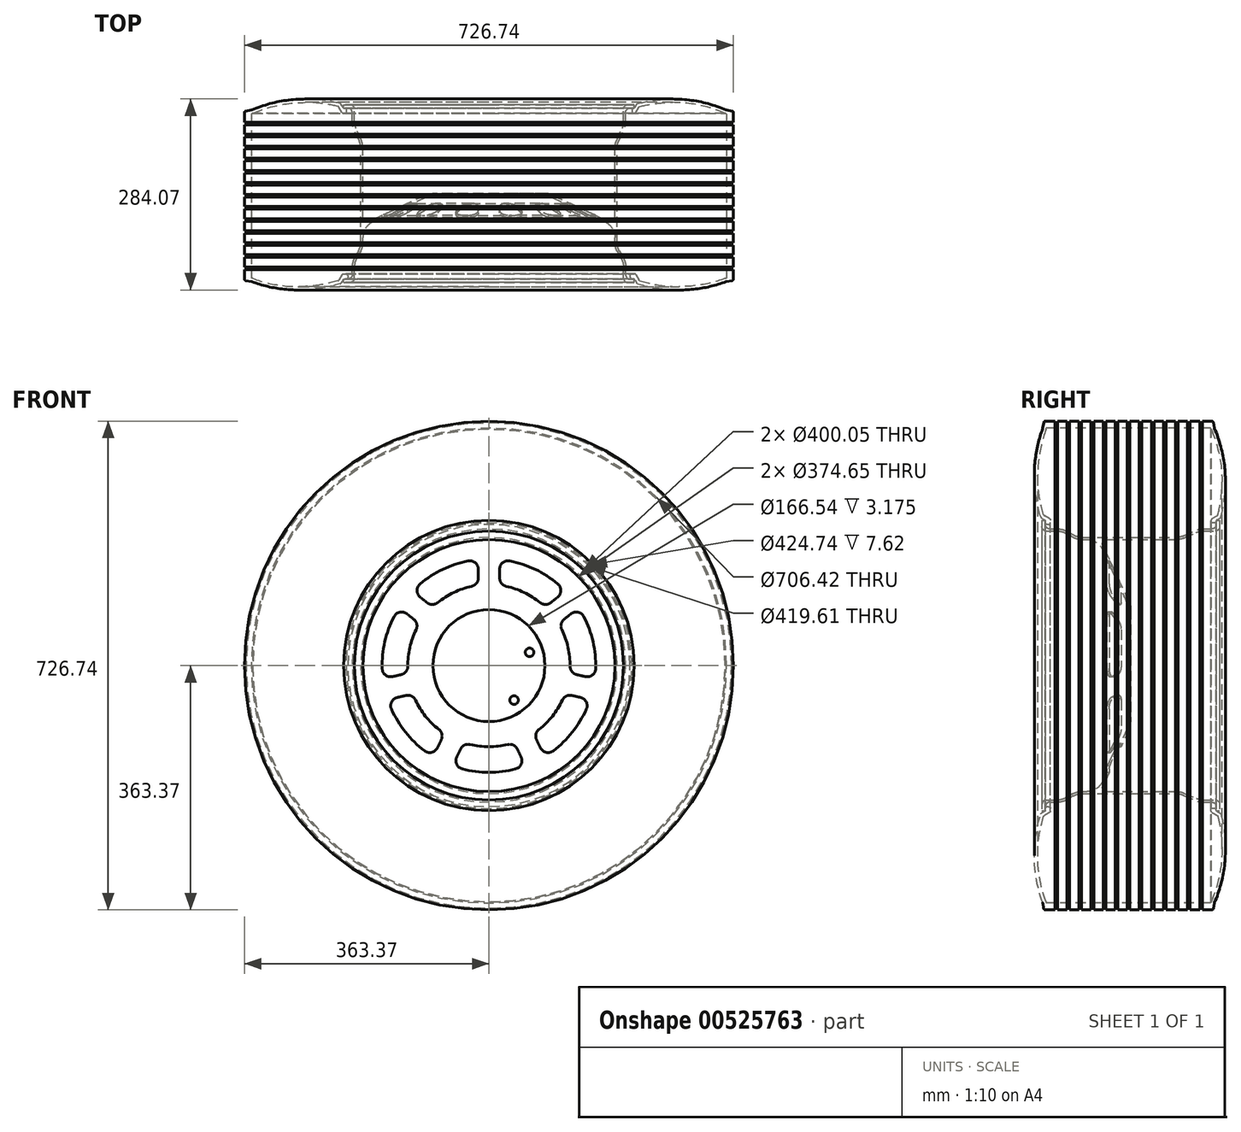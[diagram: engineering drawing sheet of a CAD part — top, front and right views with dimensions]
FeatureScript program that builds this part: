
annotation { "Feature Type Name" : "Feature", "Feature Type Description" : "" }
export const myFeature = defineFeature(function(context is Context, id is Id, definition is map)
    precondition{}
    {
        {
            var Q0;
            Q0=qCreatedBy(makeId("Top.planeOp"),FACE);
            var sketch = newSketch(context, id + "F0", { "sketchPlane" : qUnion([Q0])});
            skLineSegment(sketch, "E0", {"start": v(0, 0) * mm, "end": v(83.27, 0) * mm});
            skLineSegment(sketch, "E1", {"start": v(94, -2.38) * mm, "end": v(172.66, -39.06) * mm});
            skLineSegment(sketch, "E2", {"start": v(200.02, -106.01) * mm, "end": v(200.02, -122.55) * mm});
            skLineSegment(sketch, "E3", {"start": v(206.38, -128.9) * mm, "end": v(215.9, -128.9) * mm});
            skLineSegment(sketch, "E4", {"start": v(215.9, -128.9) * mm, "end": v(215.9, -123.82) * mm});
            skLineSegment(sketch, "E5", {"start": v(215.9, -123.82) * mm, "end": v(209.55, -123.82) * mm});
            skLineSegment(sketch, "E6", {"start": v(190.5, -69.45) * mm, "end": v(190.5, 70.8) * mm});
            skLineSegment(sketch, "E7", {"start": v(192.69, 81.13) * mm, "end": v(202.65, 103.54) * mm});
            skLineSegment(sketch, "E8", {"start": v(203.2, 106.12) * mm, "end": v(203.2, 123.83) * mm});
            skLineSegment(sketch, "E9", {"start": v(209.55, 130.18) * mm, "end": v(215.9, 130.18) * mm});
            skLineSegment(sketch, "E10", {"start": v(215.9, 130.18) * mm, "end": v(215.9, 135.26) * mm});
            skLineSegment(sketch, "E11", {"start": v(215.9, 135.26) * mm, "end": v(206.37, 135.26) * mm});
            skLineSegment(sketch, "E12", {"start": v(200.03, 128.9) * mm, "end": v(200.03, 110.84) * mm});
            skLineSegment(sketch, "E13", {"start": v(197.84, 100.52) * mm, "end": v(189.51, 81.8) * mm});
            skLineSegment(sketch, "E14", {"start": v(187.33, 71.48) * mm, "end": v(187.33, -32.43) * mm});
            skLineSegment(sketch, "E15", {"start": v(178.3, -38.18) * mm, "end": v(94.7, 0.8) * mm});
            skLineSegment(sketch, "E16", {"start": v(83.97, 3.18) * mm, "end": v(0, 3.17) * mm});
            skLineSegment(sketch, "E17", {"start": v(0, 3.17) * mm, "end": v(0, 0) * mm});
            skPoint(sketch, "E18.end.orphan", {"position": v(203.2, -45.9) * mm});
            skLineSegment(sketch, "E19", {"start": v(190.67, -82.9) * mm, "end": v(196.68, -93.41) * mm});
            skLineSegment(sketch, "E20", {"start": v(193.85, -82.06) * mm, "end": v(199.85, -92.57) * mm});
            skLineSegment(sketch, "E21", {"start": v(203.2, -105.17) * mm, "end": v(203.2, -117.47) * mm});
            skLineSegment(sketch, "E22.trimOffspring", {"start": v(187.33, -62.08) * mm, "end": v(187.33, -70.3) * mm});
            skPoint(sketch, "E23", {"position": v(190.5, 0) * mm});
            skPoint(sketch, "E24", {"position": v(190.5, -76.2) * mm});
            skPoint(sketch, "E25.visualSharp", {"position": v(88.9, 0) * mm});
            skArc(sketch, "E25.filletArc", {"start": v(94, -2.38) * mm, "mid": v(88.77, -0.6) * mm, "end": v(83.27, 0) * mm});
            skPoint(sketch, "E26.visualSharp", {"position": v(89.6, 3.18) * mm});
            skArc(sketch, "E26.filletArc", {"start": v(94.7, 0.8) * mm, "mid": v(89.47, 2.57) * mm, "end": v(83.97, 3.18) * mm});
            skPoint(sketch, "E27.visualSharp", {"position": v(187.33, -45.9) * mm});
            skArc(sketch, "E27.filletArc", {"start": v(187.32, -62.08) * mm, "mid": v(183.35, -48.43) * mm, "end": v(172.66, -39.06) * mm});
            skPoint(sketch, "E28.visualSharp", {"position": v(187.33, -42.4) * mm});
            skArc(sketch, "E28.filletArc", {"start": v(178.3, -38.18) * mm, "mid": v(184.39, -37.78) * mm, "end": v(187.33, -32.43) * mm});
            skArc(sketch, "E29.filletArc", {"start": v(190.5, -69.45) * mm, "mid": v(191.35, -75.97) * mm, "end": v(193.85, -82.06) * mm});
            skPoint(sketch, "E30.visualSharp", {"position": v(187.33, -77.04) * mm});
            skArc(sketch, "E30.filletArc", {"start": v(187.33, -70.3) * mm, "mid": v(188.18, -76.82) * mm, "end": v(190.67, -82.9) * mm});
            skPoint(sketch, "E31.visualSharp", {"position": v(200.02, -99.27) * mm});
            skArc(sketch, "E31.filletArc", {"start": v(200.02, -106.01) * mm, "mid": v(199.17, -99.5) * mm, "end": v(196.68, -93.41) * mm});
            skPoint(sketch, "E32.visualSharp", {"position": v(203.2, -98.42) * mm});
            skArc(sketch, "E32.filletArc", {"start": v(203.2, -105.17) * mm, "mid": v(202.35, -98.65) * mm, "end": v(199.85, -92.57) * mm});
            skPoint(sketch, "E33.visualSharp", {"position": v(190.5, 76.2) * mm});
            skArc(sketch, "E33.filletArc", {"start": v(192.69, 81.13) * mm, "mid": v(191.05, 76.08) * mm, "end": v(190.5, 70.8) * mm});
            skPoint(sketch, "E34.visualSharp", {"position": v(187.33, 76.87) * mm});
            skArc(sketch, "E34.filletArc", {"start": v(189.51, 81.8) * mm, "mid": v(187.88, 76.76) * mm, "end": v(187.33, 71.48) * mm});
            skPoint(sketch, "E35.visualSharp", {"position": v(200.03, 105.45) * mm});
            skArc(sketch, "E35.filletArc", {"start": v(197.84, 100.52) * mm, "mid": v(199.47, 105.57) * mm, "end": v(200.03, 110.84) * mm});
            skPoint(sketch, "E36.visualSharp", {"position": v(203.2, 104.78) * mm});
            skArc(sketch, "E36.filletArc", {"start": v(202.65, 103.54) * mm, "mid": v(203.06, 104.8) * mm, "end": v(203.2, 106.12) * mm});
            skPoint(sketch, "E37.visualSharp", {"position": v(203.2, 130.18) * mm});
            skArc(sketch, "E37.filletArc", {"start": v(209.55, 130.18) * mm, "mid": v(205.06, 128.32) * mm, "end": v(203.2, 123.83) * mm});
            skPoint(sketch, "E38.visualSharp", {"position": v(200.03, 135.26) * mm});
            skArc(sketch, "E38.filletArc", {"start": v(206.37, 135.26) * mm, "mid": v(201.88, 133.4) * mm, "end": v(200.02, 128.9) * mm});
            skPoint(sketch, "E39.visualSharp", {"position": v(203.2, -123.82) * mm});
            skArc(sketch, "E39.filletArc", {"start": v(203.2, -117.47) * mm, "mid": v(205.06, -121.97) * mm, "end": v(209.55, -123.82) * mm});
            skPoint(sketch, "E40.visualSharp", {"position": v(200.02, -128.9) * mm});
            skArc(sketch, "E40.filletArc", {"start": v(200.03, -122.55) * mm, "mid": v(201.88, -127.05) * mm, "end": v(206.38, -128.9) * mm});
            skSolve(sketch);
        }
        {
            var Q0;
            Q0=qCreatedBy(makeId("Top.planeOp"),FACE);
            var sketch = newSketch(context, id + "F1", { "sketchPlane" : qUnion([Q0])});
            skLineSegment(sketch, "E41", {"start": v(212.37, 130.18) * mm, "end": v(214.69, 130.18) * mm});
            skLineSegment(sketch, "E42", {"start": v(216.89, 131.45) * mm, "end": v(219.44, 135.86) * mm});
            skArc(sketch, "E43", {"start": v(352.47, 127.57) * mm, "mid": v(287.52, 143.27) * mm, "end": v(220.99, 137.05) * mm});
            skLineSegment(sketch, "E44", {"start": v(353.03, 127.4) * mm, "end": v(361.27, 125.95) * mm});
            skLineSegment(sketch, "E45", {"start": v(363.37, 123.45) * mm, "end": v(363.37, 109.33) * mm});
            skLineSegment(sketch, "E46", {"start": v(361.27, -126.25) * mm, "end": v(352.96, -127.71) * mm});
            skArc(sketch, "E47", {"start": v(220.9, -130.73) * mm, "mid": v(286.96, -140.23) * mm, "end": v(352.53, -127.83) * mm});
            skLineSegment(sketch, "E48", {"start": v(219.47, -129.57) * mm, "end": v(216.89, -125.1) * mm});
            skLineSegment(sketch, "E49", {"start": v(214.69, -123.82) * mm, "end": v(212.34, -123.82) * mm});
            skLineSegment(sketch, "E50", {"start": v(212.37, 130.18) * mm, "end": v(212.37, 122.56) * mm});
            skLineSegment(sketch, "E51", {"start": v(212.37, 122.56) * mm, "end": v(216.15, 122.56) * mm});
            skLineSegment(sketch, "E52", {"start": v(218.35, 123.83) * mm, "end": v(222.77, 131.48) * mm});
            skArc(sketch, "E53", {"start": v(351, 122.67) * mm, "mid": v(288.5, 138.1) * mm, "end": v(224.35, 132.67) * mm});
            skLineSegment(sketch, "E54", {"start": v(351.11, 122.58) * mm, "end": v(351.57, 122.5) * mm});
            skLineSegment(sketch, "E55", {"start": v(353.2, 120.08) * mm, "end": v(353.2, -122.09) * mm});
            skLineSegment(sketch, "E56", {"start": v(352.8, -122.59) * mm, "end": v(351.63, -122.8) * mm});
            skArc(sketch, "E57", {"start": v(224.34, -126.48) * mm, "mid": v(288.06, -135.12) * mm, "end": v(351.2, -122.9) * mm});
            skLineSegment(sketch, "E58", {"start": v(222.88, -125.32) * mm, "end": v(218.35, -117.47) * mm});
            skLineSegment(sketch, "E59", {"start": v(216.15, -116.2) * mm, "end": v(212.34, -116.2) * mm});
            skLineSegment(sketch, "E60", {"start": v(209.8, -118.74) * mm, "end": v(209.8, -121.28) * mm});
            skPoint(sketch, "E61.visualSharp", {"position": v(217.62, 122.56) * mm});
            skArc(sketch, "E61.filletArc", {"start": v(216.15, 122.56) * mm, "mid": v(217.42, 122.9) * mm, "end": v(218.35, 123.83) * mm});
            skPoint(sketch, "E62.visualSharp", {"position": v(216.15, 130.18) * mm});
            skArc(sketch, "E62.filletArc", {"start": v(214.69, 130.18) * mm, "mid": v(215.96, 130.52) * mm, "end": v(216.89, 131.45) * mm});
            skPoint(sketch, "E63.visualSharp", {"position": v(223.3, 132.4) * mm});
            skArc(sketch, "E63.filletArc", {"start": v(224.35, 132.67) * mm, "mid": v(223.44, 132.23) * mm, "end": v(222.77, 131.48) * mm});
            skPoint(sketch, "E64.visualSharp", {"position": v(219.96, 136.77) * mm});
            skArc(sketch, "E64.filletArc", {"start": v(220.99, 137.05) * mm, "mid": v(220.1, 136.6) * mm, "end": v(219.44, 135.86) * mm});
            skPoint(sketch, "E65.visualSharp", {"position": v(352.74, 127.46) * mm});
            skArc(sketch, "E65.filletArc", {"start": v(352.47, 127.57) * mm, "mid": v(352.74, 127.47) * mm, "end": v(353.03, 127.4) * mm});
            skPoint(sketch, "E66.visualSharp", {"position": v(351.28, 122.56) * mm});
            skArc(sketch, "E66.filletArc", {"start": v(351, 122.67) * mm, "mid": v(351.28, 122.57) * mm, "end": v(351.57, 122.5) * mm});
            skPoint(sketch, "E67.visualSharp", {"position": v(353.2, 122.21) * mm});
            skArc(sketch, "E67.filletArc", {"start": v(353.2, 120.08) * mm, "mid": v(352.62, 121.72) * mm, "end": v(351.11, 122.58) * mm});
            skPoint(sketch, "E68.visualSharp", {"position": v(363.37, 125.58) * mm});
            skArc(sketch, "E68.filletArc", {"start": v(363.37, 123.45) * mm, "mid": v(362.78, 125.08) * mm, "end": v(361.27, 125.95) * mm});
            skPoint(sketch, "E69.visualSharp", {"position": v(363.37, -125.88) * mm});
            skArc(sketch, "E69.filletArc", {"start": v(361.27, -126.25) * mm, "mid": v(362.78, -125.38) * mm, "end": v(363.37, -123.75) * mm});
            skPoint(sketch, "E70.visualSharp", {"position": v(353.2, -122.51) * mm});
            skArc(sketch, "E70.filletArc", {"start": v(352.8, -122.59) * mm, "mid": v(353.1, -122.41) * mm, "end": v(353.2, -122.09) * mm});
            skPoint(sketch, "E71.visualSharp", {"position": v(352.74, -127.75) * mm});
            skArc(sketch, "E71.filletArc", {"start": v(352.96, -127.71) * mm, "mid": v(352.74, -127.76) * mm, "end": v(352.53, -127.83) * mm});
            skPoint(sketch, "E72.visualSharp", {"position": v(351.4, -122.83) * mm});
            skArc(sketch, "E72.filletArc", {"start": v(351.63, -122.8) * mm, "mid": v(351.4, -122.84) * mm, "end": v(351.2, -122.9) * mm});
            skPoint(sketch, "E73.visualSharp", {"position": v(219.96, -130.42) * mm});
            skArc(sketch, "E73.filletArc", {"start": v(219.47, -129.57) * mm, "mid": v(220.08, -130.28) * mm, "end": v(220.9, -130.73) * mm});
            skPoint(sketch, "E74.visualSharp", {"position": v(223.38, -126.18) * mm});
            skArc(sketch, "E74.filletArc", {"start": v(222.88, -125.32) * mm, "mid": v(223.5, -126.03) * mm, "end": v(224.34, -126.48) * mm});
            skPoint(sketch, "E75.visualSharp", {"position": v(216.15, -123.82) * mm});
            skArc(sketch, "E75.filletArc", {"start": v(216.89, -125.1) * mm, "mid": v(215.96, -124.17) * mm, "end": v(214.69, -123.82) * mm});
            skPoint(sketch, "E76.visualSharp", {"position": v(209.8, -116.2) * mm});
            skArc(sketch, "E76.filletArc", {"start": v(212.34, -116.2) * mm, "mid": v(210.55, -116.95) * mm, "end": v(209.8, -118.74) * mm});
            skPoint(sketch, "E77.visualSharp", {"position": v(217.62, -116.2) * mm});
            skArc(sketch, "E77.filletArc", {"start": v(218.35, -117.47) * mm, "mid": v(217.42, -116.55) * mm, "end": v(216.15, -116.2) * mm});
            skPoint(sketch, "E78.visualSharp", {"position": v(209.8, -123.82) * mm});
            skArc(sketch, "E78.filletArc", {"start": v(209.8, -121.28) * mm, "mid": v(210.55, -123.08) * mm, "end": v(212.34, -123.82) * mm});
            skLineSegment(sketch, "E79.bottom", {"start": v(363.37, 109.33) * mm, "end": v(360.83, 109.33) * mm});
            skLineSegment(sketch, "E79.top", {"start": v(363.37, 105.52) * mm, "end": v(360.83, 105.52) * mm});
            skLineSegment(sketch, "E79.right", {"start": v(360.83, 109.33) * mm, "end": v(360.83, 105.52) * mm});
            skLineSegment(sketch, "E80.bottom", {"start": v(363.37, 91.4) * mm, "end": v(360.83, 91.4) * mm});
            skLineSegment(sketch, "E80.top", {"start": v(363.37, 87.6) * mm, "end": v(360.83, 87.6) * mm});
            skLineSegment(sketch, "E80.right", {"start": v(360.83, 91.4) * mm, "end": v(360.83, 87.6) * mm});
            skLineSegment(sketch, "E81.bottom", {"start": v(363.37, 73.47) * mm, "end": v(360.83, 73.47) * mm});
            skLineSegment(sketch, "E81.top", {"start": v(363.37, 69.66) * mm, "end": v(360.83, 69.66) * mm});
            skLineSegment(sketch, "E81.right", {"start": v(360.83, 73.47) * mm, "end": v(360.83, 69.66) * mm});
            skLineSegment(sketch, "E82.bottom", {"start": v(363.37, 55.54) * mm, "end": v(360.83, 55.54) * mm});
            skLineSegment(sketch, "E82.top", {"start": v(363.37, 51.73) * mm, "end": v(360.83, 51.73) * mm});
            skLineSegment(sketch, "E82.right", {"start": v(360.83, 55.54) * mm, "end": v(360.83, 51.73) * mm});
            skLineSegment(sketch, "E83.bottom", {"start": v(363.37, 37.61) * mm, "end": v(360.83, 37.61) * mm});
            skLineSegment(sketch, "E83.top", {"start": v(363.37, 33.8) * mm, "end": v(360.83, 33.8) * mm});
            skLineSegment(sketch, "E83.right", {"start": v(360.83, 37.61) * mm, "end": v(360.83, 33.8) * mm});
            skLineSegment(sketch, "E84.bottom", {"start": v(363.37, 19.68) * mm, "end": v(360.83, 19.68) * mm});
            skLineSegment(sketch, "E84.top", {"start": v(363.37, 15.87) * mm, "end": v(360.83, 15.87) * mm});
            skLineSegment(sketch, "E84.right", {"start": v(360.83, 19.68) * mm, "end": v(360.83, 15.87) * mm});
            skLineSegment(sketch, "E85.bottom", {"start": v(363.37, 1.75) * mm, "end": v(360.83, 1.75) * mm});
            skLineSegment(sketch, "E85.top", {"start": v(363.37, -2.06) * mm, "end": v(360.83, -2.06) * mm});
            skLineSegment(sketch, "E85.right", {"start": v(360.83, 1.75) * mm, "end": v(360.83, -2.06) * mm});
            skLineSegment(sketch, "E86.bottom", {"start": v(363.37, -16.17) * mm, "end": v(360.83, -16.17) * mm});
            skLineSegment(sketch, "E86.top", {"start": v(363.37, -19.98) * mm, "end": v(360.83, -19.98) * mm});
            skLineSegment(sketch, "E86.right", {"start": v(360.83, -16.17) * mm, "end": v(360.83, -19.98) * mm});
            skLineSegment(sketch, "E87.bottom", {"start": v(363.37, -34.1) * mm, "end": v(360.83, -34.1) * mm});
            skLineSegment(sketch, "E87.top", {"start": v(363.37, -37.91) * mm, "end": v(360.83, -37.91) * mm});
            skLineSegment(sketch, "E87.right", {"start": v(360.83, -34.1) * mm, "end": v(360.83, -37.91) * mm});
            skLineSegment(sketch, "E88.bottom", {"start": v(363.37, -52.03) * mm, "end": v(360.83, -52.03) * mm});
            skLineSegment(sketch, "E88.top", {"start": v(363.37, -55.84) * mm, "end": v(360.83, -55.84) * mm});
            skLineSegment(sketch, "E88.right", {"start": v(360.83, -52.03) * mm, "end": v(360.83, -55.84) * mm});
            skLineSegment(sketch, "E89.bottom", {"start": v(363.37, -69.96) * mm, "end": v(360.83, -69.96) * mm});
            skLineSegment(sketch, "E89.top", {"start": v(363.37, -73.77) * mm, "end": v(360.83, -73.77) * mm});
            skLineSegment(sketch, "E89.right", {"start": v(360.83, -69.96) * mm, "end": v(360.83, -73.77) * mm});
            skLineSegment(sketch, "E90.bottom", {"start": v(363.37, -87.9) * mm, "end": v(360.83, -87.9) * mm});
            skLineSegment(sketch, "E90.top", {"start": v(363.37, -91.7) * mm, "end": v(360.83, -91.7) * mm});
            skLineSegment(sketch, "E90.right", {"start": v(360.83, -87.9) * mm, "end": v(360.83, -91.7) * mm});
            skLineSegment(sketch, "E91.bottom", {"start": v(363.37, -105.82) * mm, "end": v(360.83, -105.82) * mm});
            skLineSegment(sketch, "E91.top", {"start": v(363.37, -109.63) * mm, "end": v(360.98, -109.63) * mm});
            skLineSegment(sketch, "E91.right", {"start": v(360.83, -105.82) * mm, "end": v(360.98, -109.63) * mm});
            skLineSegment(sketch, "E92.trimOffspring", {"start": v(363.37, 105.52) * mm, "end": v(363.37, 91.4) * mm});
            skLineSegment(sketch, "E93.trimOffspring", {"start": v(363.37, 87.6) * mm, "end": v(363.37, 73.47) * mm});
            skLineSegment(sketch, "E94.trimOffspring", {"start": v(363.37, 69.66) * mm, "end": v(363.37, 55.54) * mm});
            skLineSegment(sketch, "E95.trimOffspring", {"start": v(363.37, 51.73) * mm, "end": v(363.37, 37.61) * mm});
            skLineSegment(sketch, "E96.trimOffspring", {"start": v(363.37, 33.8) * mm, "end": v(363.37, 19.68) * mm});
            skLineSegment(sketch, "E97.trimOffspring", {"start": v(363.37, 15.87) * mm, "end": v(363.37, 1.75) * mm});
            skLineSegment(sketch, "E98.trimOffspring", {"start": v(363.37, -2.06) * mm, "end": v(363.37, -16.17) * mm});
            skLineSegment(sketch, "E99.trimOffspring", {"start": v(363.37, -19.98) * mm, "end": v(363.37, -34.1) * mm});
            skLineSegment(sketch, "E100.trimOffspring", {"start": v(363.37, -37.91) * mm, "end": v(363.37, -52.03) * mm});
            skLineSegment(sketch, "E101.trimOffspring", {"start": v(363.37, -73.77) * mm, "end": v(363.37, -87.9) * mm});
            skLineSegment(sketch, "E102.trimOffspring", {"start": v(363.37, -55.84) * mm, "end": v(363.37, -69.96) * mm});
            skLineSegment(sketch, "E103.trimOffspring", {"start": v(363.37, -109.63) * mm, "end": v(363.37, -123.75) * mm});
            skLineSegment(sketch, "E104.trimOffspring", {"start": v(363.37, -91.7) * mm, "end": v(363.37, -105.82) * mm});
            skLineSegment(sketch, "E105", {"start": v(0, 0) * mm, "end": v(0, 58.12) * mm, "construction": true});
            skSolve(sketch);
        }
        {
            var Q0;
            Q0=makeQuery(id+"F0.imprint","IMPRINT",FACE,{"disambiguationData":[TD([[makeQuery(id+"F0.imprint","IMPRINT",EDGE,{"derivedFrom":sQuery(id+"F0.wireOp",EDGE,"E0")}),1.0]])]});
            var Q1;
            Q1=sQuery(id+"F0.wireOp",EDGE,"E17");
            revolve(context, id + "F2", {"entities" : qUnion([Q0]), "axis" : qUnion([Q1]), "revolveType" : RevolveType.FULL});
        }
        {
            var Q0;
            Q0=makeQuery(id+"F2.opRevolve","SWEPT_FACE",FACE,{"disambiguationData":[OSD([sQuery(id+"F0.wireOp",EDGE,"E0")])]});
            var sketch = newSketch(context, id + "F3", { "sketchPlane" : qUnion([Q0])});
            skCircle(sketch, "E106", {"center": v(0, 0) * mm, "radius": 28.57 * mm});
            skCircle(sketch, "E107", {"center": v(0, 0) * mm, "radius": 63.5 * mm});
            skCircle(sketch, "E108", {"center": v(0, 63.5) * mm, "radius": 6.35 * mm});
            skCircle(sketch, "E109", {"center": v(-60.4, 19.62) * mm, "radius": 6.35 * mm});
            skCircle(sketch, "E110", {"center": v(-37.32, -51.37) * mm, "radius": 6.35 * mm});
            skCircle(sketch, "E111", {"center": v(37.32, -51.37) * mm, "radius": 6.35 * mm});
            skCircle(sketch, "E112", {"center": v(60.4, 19.62) * mm, "radius": 6.35 * mm});
            skLineSegment(sketch, "E113", {"start": v(0, 63.5) * mm, "end": v(0, 0) * mm, "construction": true});
            skLineSegment(sketch, "E114", {"start": v(60.4, 19.62) * mm, "end": v(0, 0) * mm, "construction": true});
            skLineSegment(sketch, "E115", {"start": v(0, 0) * mm, "end": v(37.32, -51.37) * mm, "construction": true});
            skLineSegment(sketch, "E116", {"start": v(0, 0) * mm, "end": v(-37.32, -51.37) * mm, "construction": true});
            skLineSegment(sketch, "E117", {"start": v(-60.4, 19.62) * mm, "end": v(0, 0) * mm, "construction": true});
            skSolve(sketch);
        }
        {
            var Q0;
            {var subQ0=sQuery(id+"F3.wireOp",EDGE,"E109");var subQ1=sQuery(id+"F3.wireOp",EDGE,"E107");var subQ2=makeQuery(id+"F3.imprint","INTERSECT",VERTEX,{"disambiguationData":[OD(0.0)],"derivedFrom":[subQ1,subQ0]});Q0=makeQuery(id+"F3.imprint","IMPRINT",FACE,{"disambiguationData":[TD([[makeQuery(id+"F3.imprint","IMPRINT",EDGE,{"disambiguationData":[TD([[subQ2,-1.0]])],"derivedFrom":subQ1}),-1.0]])]});}
            var Q1;
            {var subQ0=sQuery(id+"F3.wireOp",EDGE,"E108");var subQ1=sQuery(id+"F3.wireOp",EDGE,"E107");var subQ2=makeQuery(id+"F3.imprint","INTERSECT",VERTEX,{"disambiguationData":[OD(0.0)],"derivedFrom":[subQ1,subQ0]});Q1=makeQuery(id+"F3.imprint","IMPRINT",FACE,{"disambiguationData":[TD([[makeQuery(id+"F3.imprint","IMPRINT",EDGE,{"disambiguationData":[TD([[subQ2,-1.0]])],"derivedFrom":subQ1}),1.0]])]});}
            var Q2;
            {var subQ0=sQuery(id+"F3.wireOp",EDGE,"E112");var subQ1=sQuery(id+"F3.wireOp",EDGE,"E107");var subQ2=makeQuery(id+"F3.imprint","INTERSECT",VERTEX,{"disambiguationData":[OD(0.0)],"derivedFrom":[subQ1,subQ0]});Q2=makeQuery(id+"F3.imprint","IMPRINT",FACE,{"disambiguationData":[TD([[makeQuery(id+"F3.imprint","IMPRINT",EDGE,{"disambiguationData":[TD([[subQ2,1.0]])],"derivedFrom":subQ1}),-1.0]])]});}
            var Q3;
            {var subQ0=sQuery(id+"F3.wireOp",EDGE,"E110");var subQ1=sQuery(id+"F3.wireOp",EDGE,"E107");var subQ2=makeQuery(id+"F3.imprint","INTERSECT",VERTEX,{"disambiguationData":[OD(0.0)],"derivedFrom":[subQ1,subQ0]});Q3=makeQuery(id+"F3.imprint","IMPRINT",FACE,{"disambiguationData":[TD([[makeQuery(id+"F3.imprint","IMPRINT",EDGE,{"disambiguationData":[TD([[subQ2,-1.0]])],"derivedFrom":subQ1}),1.0]])]});}
            var Q4;
            {var subQ0=sQuery(id+"F3.wireOp",EDGE,"E111");var subQ1=sQuery(id+"F3.wireOp",EDGE,"E107");var subQ2=makeQuery(id+"F3.imprint","INTERSECT",VERTEX,{"disambiguationData":[OD(0.0)],"derivedFrom":[subQ1,subQ0]});Q4=makeQuery(id+"F3.imprint","IMPRINT",FACE,{"disambiguationData":[TD([[makeQuery(id+"F3.imprint","IMPRINT",EDGE,{"disambiguationData":[TD([[subQ2,-1.0]])],"derivedFrom":subQ1}),1.0]])]});}
            var Q5;
            {var subQ0=sQuery(id+"F3.wireOp",EDGE,"E111");var subQ1=sQuery(id+"F3.wireOp",EDGE,"E107");var subQ2=makeQuery(id+"F3.imprint","INTERSECT",VERTEX,{"disambiguationData":[OD(0.0)],"derivedFrom":[subQ1,subQ0]});Q5=makeQuery(id+"F3.imprint","IMPRINT",FACE,{"disambiguationData":[TD([[makeQuery(id+"F3.imprint","IMPRINT",EDGE,{"disambiguationData":[TD([[subQ2,-1.0]])],"derivedFrom":subQ1}),-1.0]])]});}
            var Q6;
            {var subQ0=sQuery(id+"F3.wireOp",EDGE,"E110");var subQ1=sQuery(id+"F3.wireOp",EDGE,"E107");var subQ2=makeQuery(id+"F3.imprint","INTERSECT",VERTEX,{"disambiguationData":[OD(0.0)],"derivedFrom":[subQ1,subQ0]});Q6=makeQuery(id+"F3.imprint","IMPRINT",FACE,{"disambiguationData":[TD([[makeQuery(id+"F3.imprint","IMPRINT",EDGE,{"disambiguationData":[TD([[subQ2,-1.0]])],"derivedFrom":subQ1}),-1.0]])]});}
            var Q7;
            {var subQ0=sQuery(id+"F3.wireOp",EDGE,"E112");var subQ1=sQuery(id+"F3.wireOp",EDGE,"E107");var subQ2=makeQuery(id+"F3.imprint","INTERSECT",VERTEX,{"disambiguationData":[OD(0.0)],"derivedFrom":[subQ1,subQ0]});Q7=makeQuery(id+"F3.imprint","IMPRINT",FACE,{"disambiguationData":[TD([[makeQuery(id+"F3.imprint","IMPRINT",EDGE,{"disambiguationData":[TD([[subQ2,1.0]])],"derivedFrom":subQ1}),1.0]])]});}
            var Q8;
            {var subQ0=sQuery(id+"F3.wireOp",EDGE,"E108");var subQ1=sQuery(id+"F3.wireOp",EDGE,"E107");var subQ2=makeQuery(id+"F3.imprint","INTERSECT",VERTEX,{"disambiguationData":[OD(0.0)],"derivedFrom":[subQ1,subQ0]});Q8=makeQuery(id+"F3.imprint","IMPRINT",FACE,{"disambiguationData":[TD([[makeQuery(id+"F3.imprint","IMPRINT",EDGE,{"disambiguationData":[TD([[subQ2,-1.0]])],"derivedFrom":subQ1}),-1.0]])]});}
            var Q9;
            {var subQ0=sQuery(id+"F3.wireOp",EDGE,"E109");var subQ1=sQuery(id+"F3.wireOp",EDGE,"E107");var subQ2=makeQuery(id+"F3.imprint","INTERSECT",VERTEX,{"disambiguationData":[OD(0.0)],"derivedFrom":[subQ1,subQ0]});Q9=makeQuery(id+"F3.imprint","IMPRINT",FACE,{"disambiguationData":[TD([[makeQuery(id+"F3.imprint","IMPRINT",EDGE,{"disambiguationData":[TD([[subQ2,-1.0]])],"derivedFrom":subQ1}),1.0]])]});}
            var Q10;
            Q10=makeQuery(id+"F3.imprint","IMPRINT",FACE,{"disambiguationData":[TD([[makeQuery(id+"F3.imprint","IMPRINT",EDGE,{"derivedFrom":sQuery(id+"F3.wireOp",EDGE,"E106")}),1.0]])]});
            extrude(context, id + "F4", {"entities" : qUnion([Q0, Q1, Q2, Q3, Q4, Q5, Q6, Q7, Q8, Q9, Q10]), "operationType" : NewBodyOperationType.REMOVE, "oppositeDirection" : true, "depth" : 25.4 * mm, "offsetDistance" : 25.4 * mm});
        }
        {
            var Q0;
            Q0=makeQuery(id+"F2.opRevolve","SWEPT_FACE",FACE,{"disambiguationData":[OSD([sQuery(id+"F0.wireOp",EDGE,"E0")])]});
            var sketch = newSketch(context, id + "F5", { "sketchPlane" : qUnion([Q0])});
            skArc(sketch, "E118", {"start": v(-141.08, 72.78) * mm, "mid": v(-154.77, 35.33) * mm, "end": v(-158.7, -4.36) * mm});
            skArc(sketch, "E119", {"start": v(76.02, 93.69) * mm, "mid": v(52.35, 108.7) * mm, "end": v(25.85, 117.85) * mm});
            skLineSegment(sketch, "E120", {"start": v(0, 0) * mm, "end": v(-124.12, 98.98) * mm, "construction": true});
            skLineSegment(sketch, "E121", {"start": v(0, 0) * mm, "end": v(-154.77, -35.33) * mm, "construction": true});
            skLineSegment(sketch, "E122", {"start": v(-154.77, -35.33) * mm, "end": v(0, 0) * mm, "construction": true});
            skLineSegment(sketch, "E123", {"start": v(-68.88, -143.03) * mm, "end": v(0, 0) * mm, "construction": true});
            skLineSegment(sketch, "E124", {"start": v(68.88, -143.03) * mm, "end": v(0, 0) * mm, "construction": true});
            skLineSegment(sketch, "E125", {"start": v(154.77, -35.33) * mm, "end": v(0, 0) * mm, "construction": true});
            skLineSegment(sketch, "E126", {"start": v(124.12, 98.98) * mm, "end": v(0, 0) * mm, "construction": true});
            skLineSegment(sketch, "E127", {"start": v(0, 158.75) * mm, "end": v(0, 0) * mm, "construction": true});
            skLineSegment(sketch, "E128", {"start": v(-15.88, 143.23) * mm, "end": v(-15.88, 130.25) * mm});
            skLineSegment(sketch, "E129", {"start": v(15.87, 143.23) * mm, "end": v(15.87, 130.25) * mm});
            skLineSegment(sketch, "E130", {"start": v(102.08, 101.71) * mm, "end": v(91.94, 93.62) * mm});
            skLineSegment(sketch, "E131", {"start": v(121.88, 76.89) * mm, "end": v(111.73, 68.8) * mm});
            skLineSegment(sketch, "E132", {"start": v(24.61, -14.52) * mm, "end": v(28.6, -22.81) * mm});
            skLineSegment(sketch, "E133", {"start": v(4, -28.3) * mm, "end": v(0, -36.59) * mm});
            skLineSegment(sketch, "E134", {"start": v(-24.61, -14.52) * mm, "end": v(-28.6, -22.81) * mm});
            skLineSegment(sketch, "E135", {"start": v(-19.63, -20.76) * mm, "end": v(-28.6, -22.81) * mm});
            skLineSegment(sketch, "E136", {"start": v(-28.47, 2.4) * mm, "end": v(-35.67, 8.14) * mm});
            skLineSegment(sketch, "E137", {"start": v(-102.08, 101.71) * mm, "end": v(-91.94, 93.62) * mm});
            skLineSegment(sketch, "E138", {"start": v(47.84, -135.93) * mm, "end": v(42.21, -124.24) * mm});
            skLineSegment(sketch, "E139", {"start": v(136.1, -47.35) * mm, "end": v(123.45, -44.46) * mm});
            skLineSegment(sketch, "E140", {"start": v(26.7, 10.19) * mm, "end": v(35.67, 8.14) * mm});
            skLineSegment(sketch, "E141", {"start": v(-143.17, -16.4) * mm, "end": v(-130.52, -13.5) * mm});
            skArc(sketch, "E142.trimOffspring", {"start": v(-31.06, 155.68) * mm, "mid": v(-68.88, 143.03) * mm, "end": v(-102.35, 121.35) * mm});
            skArc(sketch, "E143.trimOffspring", {"start": v(-144.87, -64.92) * mm, "mid": v(-124.12, -98.98) * mm, "end": v(-95.53, -126.79) * mm});
            skArc(sketch, "E144.trimOffspring", {"start": v(-39.56, -153.74) * mm, "mid": v(0, -158.75) * mm, "end": v(39.56, -153.74) * mm});
            skArc(sketch, "E145.trimOffspring", {"start": v(95.53, -126.79) * mm, "mid": v(124.12, -98.98) * mm, "end": v(144.87, -64.92) * mm});
            skArc(sketch, "E146.trimOffspring", {"start": v(158.7, -4.36) * mm, "mid": v(154.77, 35.33) * mm, "end": v(141.08, 72.78) * mm});
            skArc(sketch, "E147.trimOffspring", {"start": v(102.35, 121.35) * mm, "mid": v(68.88, 143.03) * mm, "end": v(31.06, 155.68) * mm});
            skPoint(sketch, "E148.visualSharp", {"position": v(157.53, -19.67) * mm});
            skArc(sketch, "E148.filletArc", {"start": v(143.17, -16.4) * mm, "mid": v(153.78, -14.05) * mm, "end": v(158.7, -4.36) * mm});
            skLineSegment(sketch, "E149.trimOffspring", {"start": v(130.52, -13.5) * mm, "end": v(143.17, -16.4) * mm});
            skLineSegment(sketch, "E150.trimOffspring", {"start": v(28.6, -22.81) * mm, "end": v(19.63, -20.76) * mm});
            skLineSegment(sketch, "E151.trimOffspring", {"start": v(35.67, 8.14) * mm, "end": v(28.47, 2.4) * mm});
            skLineSegment(sketch, "E152.trimOffspring", {"start": v(15.88, 32.96) * mm, "end": v(8.68, 27.23) * mm});
            skArc(sketch, "E153.trimOffspring", {"start": v(120.65, -1.02) * mm, "mid": v(117.63, 26.85) * mm, "end": v(108.26, 53.26) * mm});
            skPoint(sketch, "E154.visualSharp", {"position": v(120.13, -11.14) * mm});
            skArc(sketch, "E154.filletArc", {"start": v(120.65, -1.02) * mm, "mid": v(123.38, -9) * mm, "end": v(130.52, -13.5) * mm});
            skPoint(sketch, "E155.visualSharp", {"position": v(103.4, 62.16) * mm});
            skArc(sketch, "E155.filletArc", {"start": v(111.73, 68.8) * mm, "mid": v(107.26, 61.64) * mm, "end": v(108.26, 53.26) * mm});
            skPoint(sketch, "E156.visualSharp", {"position": v(133.4, 86.07) * mm});
            skArc(sketch, "E156.filletArc", {"start": v(141.08, 72.78) * mm, "mid": v(132.45, 79.38) * mm, "end": v(121.88, 76.89) * mm});
            skPoint(sketch, "E157.visualSharp", {"position": v(83.6, 86.98) * mm});
            skArc(sketch, "E157.filletArc", {"start": v(76.02, 93.69) * mm, "mid": v(83.97, 90.85) * mm, "end": v(91.94, 93.62) * mm});
            skPoint(sketch, "E158.visualSharp", {"position": v(113.6, 110.9) * mm});
            skArc(sketch, "E158.filletArc", {"start": v(102.08, 101.71) * mm, "mid": v(106.86, 111.47) * mm, "end": v(102.35, 121.35) * mm});
            skArc(sketch, "E159.trimOffspring", {"start": v(-25.85, 117.85) * mm, "mid": v(-52.35, 108.7) * mm, "end": v(-76.02, 93.69) * mm});
            skLineSegment(sketch, "E160.trimOffspring", {"start": v(15.88, 32.96) * mm, "end": v(15.88, 23.76) * mm});
            skLineSegment(sketch, "E161.trimOffspring", {"start": v(-15.87, 32.96) * mm, "end": v(-15.87, 23.76) * mm});
            skLineSegment(sketch, "E162.trimOffspring", {"start": v(-15.87, 32.96) * mm, "end": v(-8.68, 27.23) * mm});
            skArc(sketch, "E163.trimOffspring", {"start": v(-108.26, 53.26) * mm, "mid": v(-117.63, 26.85) * mm, "end": v(-120.65, -1.02) * mm});
            skLineSegment(sketch, "E164.trimOffspring", {"start": v(-111.73, 68.8) * mm, "end": v(-121.88, 76.89) * mm});
            skLineSegment(sketch, "E165.trimOffspring", {"start": v(-35.67, 8.14) * mm, "end": v(-26.7, 10.19) * mm});
            skArc(sketch, "E166.trimOffspring", {"start": v(-109.14, -51.43) * mm, "mid": v(-94.33, -75.22) * mm, "end": v(-74.43, -94.96) * mm});
            skLineSegment(sketch, "E167.trimOffspring", {"start": v(-123.45, -44.46) * mm, "end": v(-136.1, -47.35) * mm});
            skArc(sketch, "E168.trimOffspring", {"start": v(-27.84, -117.4) * mm, "mid": v(0, -120.65) * mm, "end": v(27.84, -117.4) * mm});
            skLineSegment(sketch, "E169.trimOffspring", {"start": v(-70.82, -110.47) * mm, "end": v(-76.45, -122.16) * mm});
            skLineSegment(sketch, "E170.trimOffspring", {"start": v(-42.21, -124.24) * mm, "end": v(-47.84, -135.93) * mm});
            skLineSegment(sketch, "E171.trimOffspring", {"start": v(0, -36.59) * mm, "end": v(-4, -28.3) * mm});
            skArc(sketch, "E172.trimOffspring", {"start": v(74.43, -94.96) * mm, "mid": v(94.33, -75.22) * mm, "end": v(109.14, -51.43) * mm});
            skLineSegment(sketch, "E173.trimOffspring", {"start": v(70.82, -110.47) * mm, "end": v(76.45, -122.16) * mm});
            skPoint(sketch, "E174.visualSharp", {"position": v(113.07, -42.1) * mm});
            skArc(sketch, "E174.filletArc", {"start": v(123.45, -44.46) * mm, "mid": v(115.07, -45.42) * mm, "end": v(109.14, -51.43) * mm});
            skPoint(sketch, "E175.visualSharp", {"position": v(150.46, -50.63) * mm});
            skArc(sketch, "E175.filletArc", {"start": v(144.87, -64.92) * mm, "mid": v(144.64, -54.06) * mm, "end": v(136.1, -47.35) * mm});
            skPoint(sketch, "E176.visualSharp", {"position": v(66.2, -100.87) * mm});
            skArc(sketch, "E176.filletArc", {"start": v(74.43, -94.96) * mm, "mid": v(69.9, -102.08) * mm, "end": v(70.82, -110.47) * mm});
            skPoint(sketch, "E177.visualSharp", {"position": v(82.84, -135.42) * mm});
            skArc(sketch, "E177.filletArc", {"start": v(76.45, -122.16) * mm, "mid": v(84.9, -128.99) * mm, "end": v(95.53, -126.79) * mm});
            skPoint(sketch, "E178.visualSharp", {"position": v(54.23, -149.2) * mm});
            skArc(sketch, "E178.filletArc", {"start": v(39.56, -153.74) * mm, "mid": v(47.92, -146.8) * mm, "end": v(47.84, -135.93) * mm});
            skPoint(sketch, "E179.visualSharp", {"position": v(37.6, -114.64) * mm});
            skArc(sketch, "E179.filletArc", {"start": v(42.21, -124.24) * mm, "mid": v(36.23, -118.29) * mm, "end": v(27.84, -117.4) * mm});
            skPoint(sketch, "E180.visualSharp", {"position": v(-37.6, -114.64) * mm});
            skArc(sketch, "E180.filletArc", {"start": v(-27.84, -117.4) * mm, "mid": v(-36.23, -118.29) * mm, "end": v(-42.21, -124.24) * mm});
            skPoint(sketch, "E181.visualSharp", {"position": v(-54.23, -149.2) * mm});
            skArc(sketch, "E181.filletArc", {"start": v(-47.84, -135.93) * mm, "mid": v(-47.92, -146.8) * mm, "end": v(-39.56, -153.74) * mm});
            skPoint(sketch, "E182.visualSharp", {"position": v(-66.2, -100.87) * mm});
            skArc(sketch, "E182.filletArc", {"start": v(-70.82, -110.47) * mm, "mid": v(-69.9, -102.08) * mm, "end": v(-74.43, -94.96) * mm});
            skPoint(sketch, "E183.visualSharp", {"position": v(-150.46, -50.63) * mm});
            skArc(sketch, "E183.filletArc", {"start": v(-136.1, -47.35) * mm, "mid": v(-144.64, -54.06) * mm, "end": v(-144.87, -64.92) * mm});
            skPoint(sketch, "E184.visualSharp", {"position": v(-82.84, -135.42) * mm});
            skArc(sketch, "E184.filletArc", {"start": v(-95.53, -126.79) * mm, "mid": v(-84.9, -128.99) * mm, "end": v(-76.45, -122.16) * mm});
            skPoint(sketch, "E185.visualSharp", {"position": v(-113.07, -42.1) * mm});
            skArc(sketch, "E185.filletArc", {"start": v(-109.14, -51.43) * mm, "mid": v(-115.07, -45.42) * mm, "end": v(-123.45, -44.46) * mm});
            skPoint(sketch, "E186.visualSharp", {"position": v(-120.13, -11.14) * mm});
            skArc(sketch, "E186.filletArc", {"start": v(-130.52, -13.5) * mm, "mid": v(-123.38, -9) * mm, "end": v(-120.65, -1.02) * mm});
            skPoint(sketch, "E187.visualSharp", {"position": v(-157.53, -19.67) * mm});
            skArc(sketch, "E187.filletArc", {"start": v(-158.7, -4.36) * mm, "mid": v(-153.78, -14.05) * mm, "end": v(-143.17, -16.4) * mm});
            skPoint(sketch, "E188.visualSharp", {"position": v(-133.4, 86.07) * mm});
            skArc(sketch, "E188.filletArc", {"start": v(-121.88, 76.89) * mm, "mid": v(-132.45, 79.38) * mm, "end": v(-141.08, 72.78) * mm});
            skPoint(sketch, "E189.visualSharp", {"position": v(-103.4, 62.16) * mm});
            skArc(sketch, "E189.filletArc", {"start": v(-108.26, 53.26) * mm, "mid": v(-107.26, 61.64) * mm, "end": v(-111.73, 68.8) * mm});
            skPoint(sketch, "E190.visualSharp", {"position": v(-113.6, 110.9) * mm});
            skArc(sketch, "E190.filletArc", {"start": v(-102.35, 121.35) * mm, "mid": v(-106.86, 111.47) * mm, "end": v(-102.08, 101.71) * mm});
            skPoint(sketch, "E191.visualSharp", {"position": v(-15.88, 119.6) * mm});
            skArc(sketch, "E191.filletArc", {"start": v(-25.85, 117.85) * mm, "mid": v(-18.68, 122.3) * mm, "end": v(-15.88, 130.25) * mm});
            skPoint(sketch, "E192.visualSharp", {"position": v(-15.88, 157.95) * mm});
            skArc(sketch, "E192.filletArc", {"start": v(-15.88, 143.23) * mm, "mid": v(-20.52, 153.05) * mm, "end": v(-31.06, 155.68) * mm});
            skPoint(sketch, "E193.visualSharp", {"position": v(-83.6, 86.98) * mm});
            skArc(sketch, "E193.filletArc", {"start": v(-91.94, 93.62) * mm, "mid": v(-83.97, 90.85) * mm, "end": v(-76.02, 93.69) * mm});
            skPoint(sketch, "E194.visualSharp", {"position": v(15.88, 157.95) * mm});
            skArc(sketch, "E194.filletArc", {"start": v(31.06, 155.68) * mm, "mid": v(20.52, 153.05) * mm, "end": v(15.87, 143.23) * mm});
            skPoint(sketch, "E195.visualSharp", {"position": v(15.87, 119.6) * mm});
            skArc(sketch, "E195.filletArc", {"start": v(15.87, 130.25) * mm, "mid": v(18.68, 122.3) * mm, "end": v(25.85, 117.85) * mm});
            skSolve(sketch);
        }
        {
            var Q0;
            Q0 = qSketchRegion(id + "F5", true);
            extrude(context, id + "F6", {"entities" : qUnion([Q0]), "operationType" : NewBodyOperationType.REMOVE, "depth" : 101.6 * mm, "offsetDistance" : 25.4 * mm});
        }
        {
            var Q0;
            Q0=makeQuery(id+"F1.imprint","IMPRINT",FACE,{"disambiguationData":[TD([[makeQuery(id+"F1.imprint","IMPRINT",EDGE,{"derivedFrom":sQuery(id+"F1.wireOp",EDGE,"E41")}),-1.0]])]});
            var Q1;
            Q1=sQuery(id+"F1.wireOp",EDGE,"E105");
            revolve(context, id + "F7", {"entities" : qUnion([Q0]), "axis" : qUnion([Q1]), "revolveType" : RevolveType.FULL});
        }
    });
